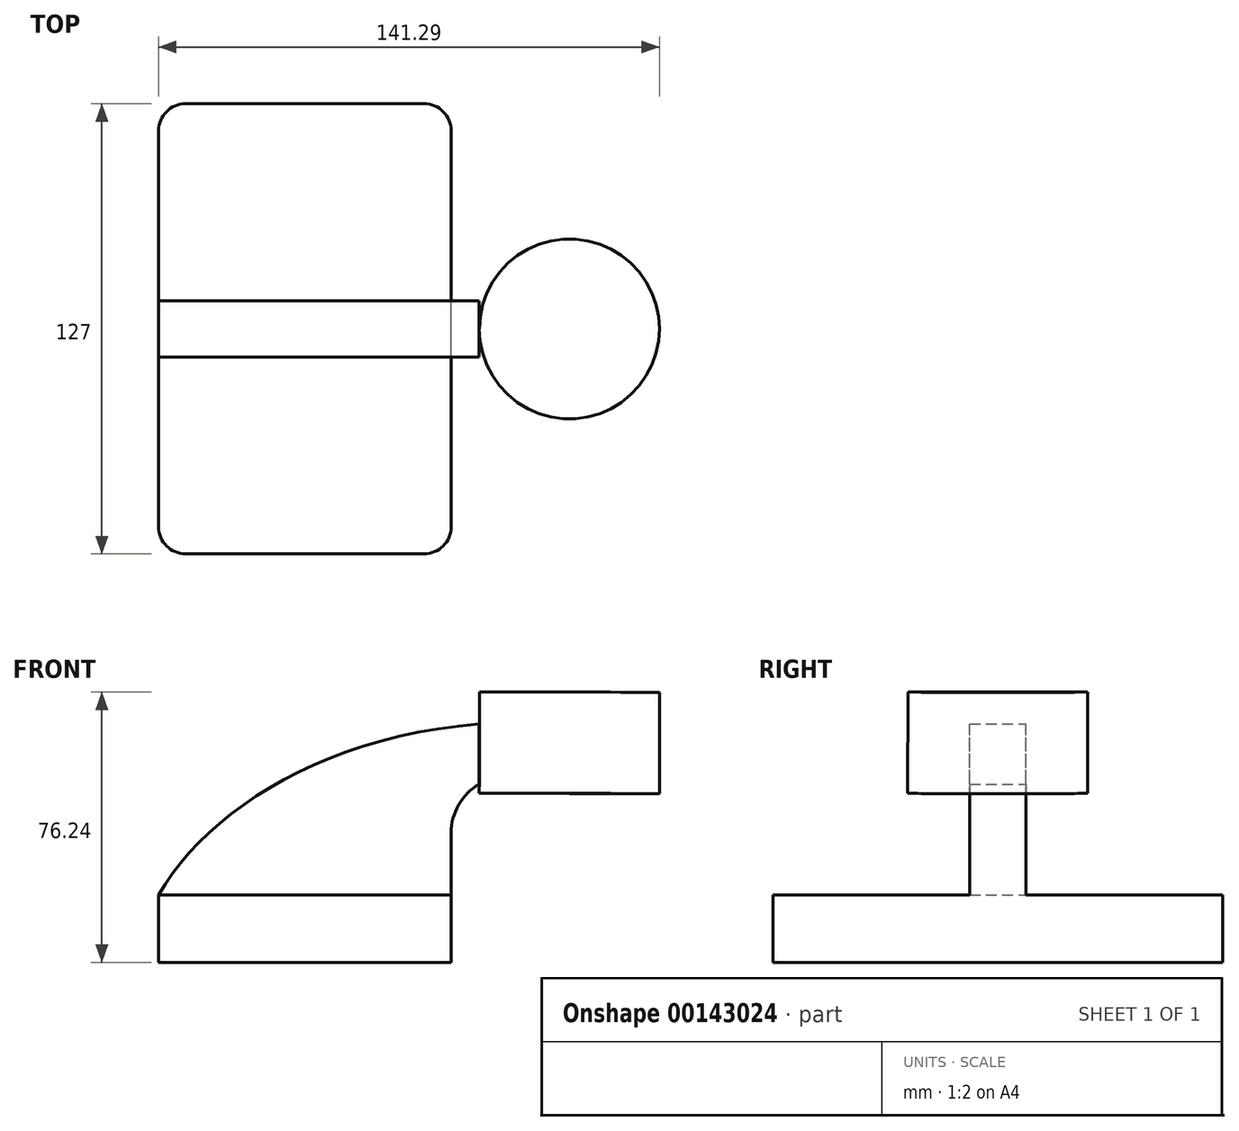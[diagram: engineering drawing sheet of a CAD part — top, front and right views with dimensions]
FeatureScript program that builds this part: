
annotation { "Feature Type Name" : "Feature", "Feature Type Description" : "" }
export const myFeature = defineFeature(function(context is Context, id is Id, definition is map)
    precondition{}
    {
        {
            var Q0;
            Q0=qCreatedBy(makeId("Front.planeOp"),FACE);
            var sketch = newSketch(context, id + "F0", { "sketchPlane" : qUnion([Q0])});
            skLineSegment(sketch, "E0.bottom", {"start": v(41.28, -9.52) * mm, "end": v(-41.28, -9.53) * mm});
            skLineSegment(sketch, "E0.top", {"start": v(41.28, 9.53) * mm, "end": v(-41.28, 9.52) * mm});
            skLineSegment(sketch, "E0.left", {"start": v(41.28, -9.52) * mm, "end": v(41.28, 9.53) * mm});
            skLineSegment(sketch, "E0.right", {"start": v(-41.28, -9.53) * mm, "end": v(-41.28, 9.52) * mm});
            skPoint(sketch, "E0.middle", {"position": v(0, 0) * mm});
            skLineSegment(sketch, "E1.bottom", {"start": v(100.01, 38.1) * mm, "end": v(49.21, 38.1) * mm});
            skLineSegment(sketch, "E1.top", {"start": v(100.01, 66.68) * mm, "end": v(49.21, 66.68) * mm});
            skLineSegment(sketch, "E1.left", {"start": v(100.01, 38.1) * mm, "end": v(100.01, 66.68) * mm});
            skLineSegment(sketch, "E1.right", {"start": v(49.21, 38.1) * mm, "end": v(49.21, 66.68) * mm});
            skPoint(sketch, "E1.middle", {"position": v(74.61, 52.39) * mm});
            skLineSegment(sketch, "E2", {"start": v(41.28, 9.53) * mm, "end": v(41.28, 27) * mm});
            skArc(sketch, "E3", {"start": v(41.28, 27) * mm, "mid": v(45.92, 38.23) * mm, "end": v(57.15, 42.88) * mm});
            skLineSegment(sketch, "E4", {"start": v(57.15, 42.88) * mm, "end": v(74.63, 42.88) * mm});
            skLineSegment(sketch, "E5.0", {"start": v(57.15, 58.75) * mm, "end": v(74.63, 58.75) * mm});
            skArc(sketch, "E5.1", {"start": v(25.4, 27) * mm, "mid": v(34.7, 49.45) * mm, "end": v(57.15, 58.75) * mm});
            skLineSegment(sketch, "E5.2", {"start": v(25.4, 9.53) * mm, "end": v(25.4, 27) * mm});
            skLineSegment(sketch, "E6", {"start": v(74.61, 38.1) * mm, "end": v(74.63, 66.68) * mm});
            skFitSpline(sketch, "E7", {"points": [v(-41.28, 9.53) * mm, v(49.21, 57.74) * mm], "startDerivative": vector(40.71, 69.45) * mm, "endDerivative": vector(136.14, 11.55) * mm});
            skSolve(sketch);
        }
        {
            var Q0;
            Q0=makeQuery(id+"F0.imprint","IMPRINT",FACE,{"disambiguationData":[TD([[makeQuery(id+"F0.imprint","IMPRINT",EDGE,{"derivedFrom":sQuery(id+"F0.wireOp",EDGE,"E0.bottom")}),-1.0]])]});
            extrude(context, id + "F1", {"entities" : qUnion([Q0]), "endBound" : BoundingType.SYMMETRIC, "depth" : 127 * mm});
        }
        {
            var Q0;
            {var subQ2=sQuery(id+"F0.wireOp",EDGE,"E5.2");Q0=makeQuery(id+"F0.imprint","IMPRINT",FACE,{"disambiguationData":[TD([[makeQuery(id+"F0.imprint","IMPRINT",EDGE,{"derivedFrom":subQ2}),1.0]])]});}
            var Q1;
            {var subQ1=sQuery(id+"F0.wireOp",EDGE,"E2");Q1=makeQuery(id+"F0.imprint","IMPRINT",FACE,{"disambiguationData":[TD([[makeQuery(id+"F0.imprint","IMPRINT",EDGE,{"derivedFrom":subQ1}),1.0]])]});}
            var Q2;
            {var subQ5=sQuery(id+"F0.wireOp",EDGE,"E4");var subQ6=sQuery(id+"F0.wireOp",EDGE,"E3");var subQ7=makeQuery(id+"F0.imprint","INTERSECT",VERTEX,{"derivedFrom":[subQ6,subQ5]});Q2=makeQuery(id+"F0.imprint","IMPRINT",FACE,{"disambiguationData":[TD([[makeQuery(id+"F0.imprint","IMPRINT",EDGE,{"disambiguationData":[TD([[subQ7,1.0]])],"derivedFrom":subQ6}),1.0]])]});}
            extrude(context, id + "F2", {"entities" : qUnion([Q0, Q1, Q2]), "operationType" : NewBodyOperationType.ADD, "endBound" : BoundingType.SYMMETRIC, "depth" : 15.88 * mm});
        }
        {
            var Q0;
            {var subQ0=sQuery(id+"F0.wireOp",EDGE,"E1.left");Q0=makeQuery(id+"F0.imprint","IMPRINT",FACE,{"disambiguationData":[TD([[makeQuery(id+"F0.imprint","IMPRINT",EDGE,{"derivedFrom":subQ0}),1.0]])]});}
            var Q1;
            Q1=sQuery(id+"F0.wireOp",EDGE,"E6");
            revolve(context, id + "F3", {"operationType" : NewBodyOperationType.ADD, "entities" : qUnion([Q0]), "axis" : qUnion([Q1]), "revolveType" : RevolveType.FULL});
        }
        {
            var Q0;
            Q0=makeQuery(id+"F1.opExtrude","CAP_EDGE",EDGE,{"disambiguationData":[OSD([sQuery(id+"F0.wireOp",EDGE,"E0.left")])],"isStart":false});
            var Q1;
            Q1=makeQuery(id+"F1.opExtrude","CAP_EDGE",EDGE,{"disambiguationData":[OSD([sQuery(id+"F0.wireOp",EDGE,"E0.right")])],"isStart":false});
            var Q2;
            Q2=makeQuery(id+"F1.opExtrude","CAP_EDGE",EDGE,{"disambiguationData":[OSD([sQuery(id+"F0.wireOp",EDGE,"E0.left")])],"isStart":true});
            var Q3;
            Q3=makeQuery(id+"F1.opExtrude","CAP_EDGE",EDGE,{"disambiguationData":[OSD([sQuery(id+"F0.wireOp",EDGE,"E0.right")])],"isStart":true});
            fillet(context, id + "F4", {"entities" : qUnion([Q0, Q1, Q2, Q3]), "radius" : 7.62 * mm, "tangentPropagation" : true, "allowEdgeOverflow" : false});
        }
    });
